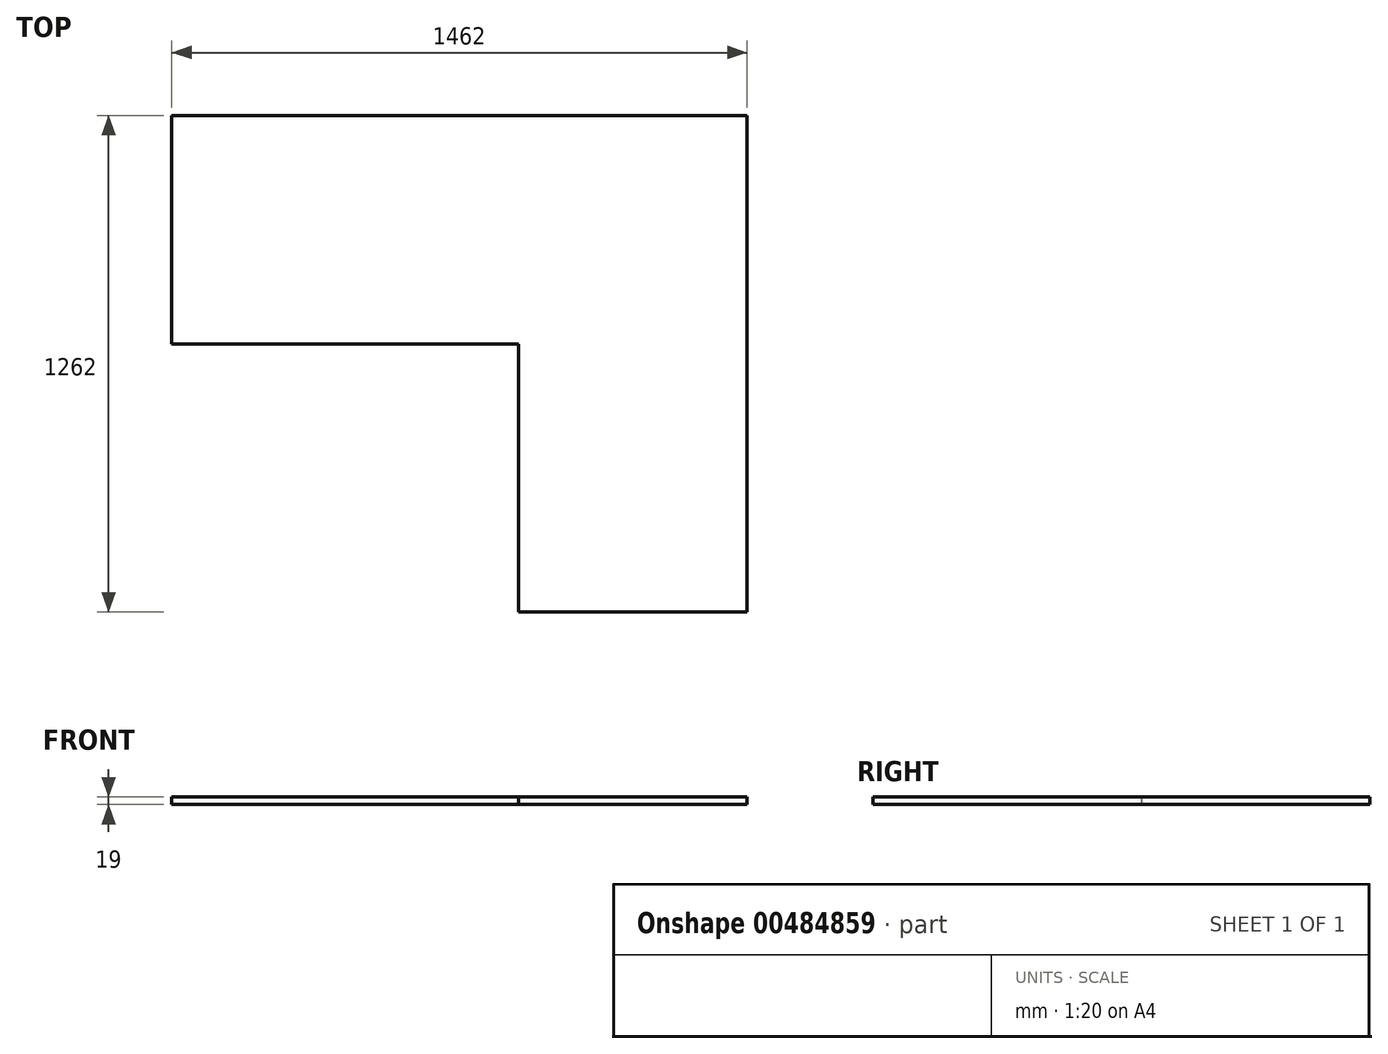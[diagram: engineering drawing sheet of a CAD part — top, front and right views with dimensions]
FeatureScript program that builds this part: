
annotation { "Feature Type Name" : "Feature", "Feature Type Description" : "" }
export const myFeature = defineFeature(function(context is Context, id is Id, definition is map)
    precondition{}
    {
        {
            var Q0;
            Q0=qCreatedBy(makeId("Top.planeOp"),FACE);
            var sketch = newSketch(context, id + "F0", { "sketchPlane" : qUnion([Q0])});
            skLineSegment(sketch, "E0.bottom", {"start": v(-147.45, 499.1) * mm, "end": v(1314.55, 499.1) * mm});
            skLineSegment(sketch, "E0.top", {"start": v(-147.45, -81.9) * mm, "end": v(1314.55, -81.9) * mm});
            skLineSegment(sketch, "E0.left", {"start": v(-147.45, 499.1) * mm, "end": v(-147.45, -81.9) * mm});
            skLineSegment(sketch, "E0.right", {"start": v(1314.55, 499.1) * mm, "end": v(1314.55, -81.9) * mm});
            skLineSegment(sketch, "E1", {"start": v(1314.55, -81.9) * mm, "end": v(1314.55, -762.9) * mm});
            skLineSegment(sketch, "E2", {"start": v(1314.55, -762.9) * mm, "end": v(733.55, -762.9) * mm});
            skLineSegment(sketch, "E3", {"start": v(733.55, -762.9) * mm, "end": v(733.55, -81.9) * mm});
            skSolve(sketch);
        }
        {
            var Q0;
            Q0 = qSketchRegion(id + "F0", true);
            extrude(context, id + "F1", {"entities" : qUnion([Q0]), "depth" : 19 * mm});
        }
    });
